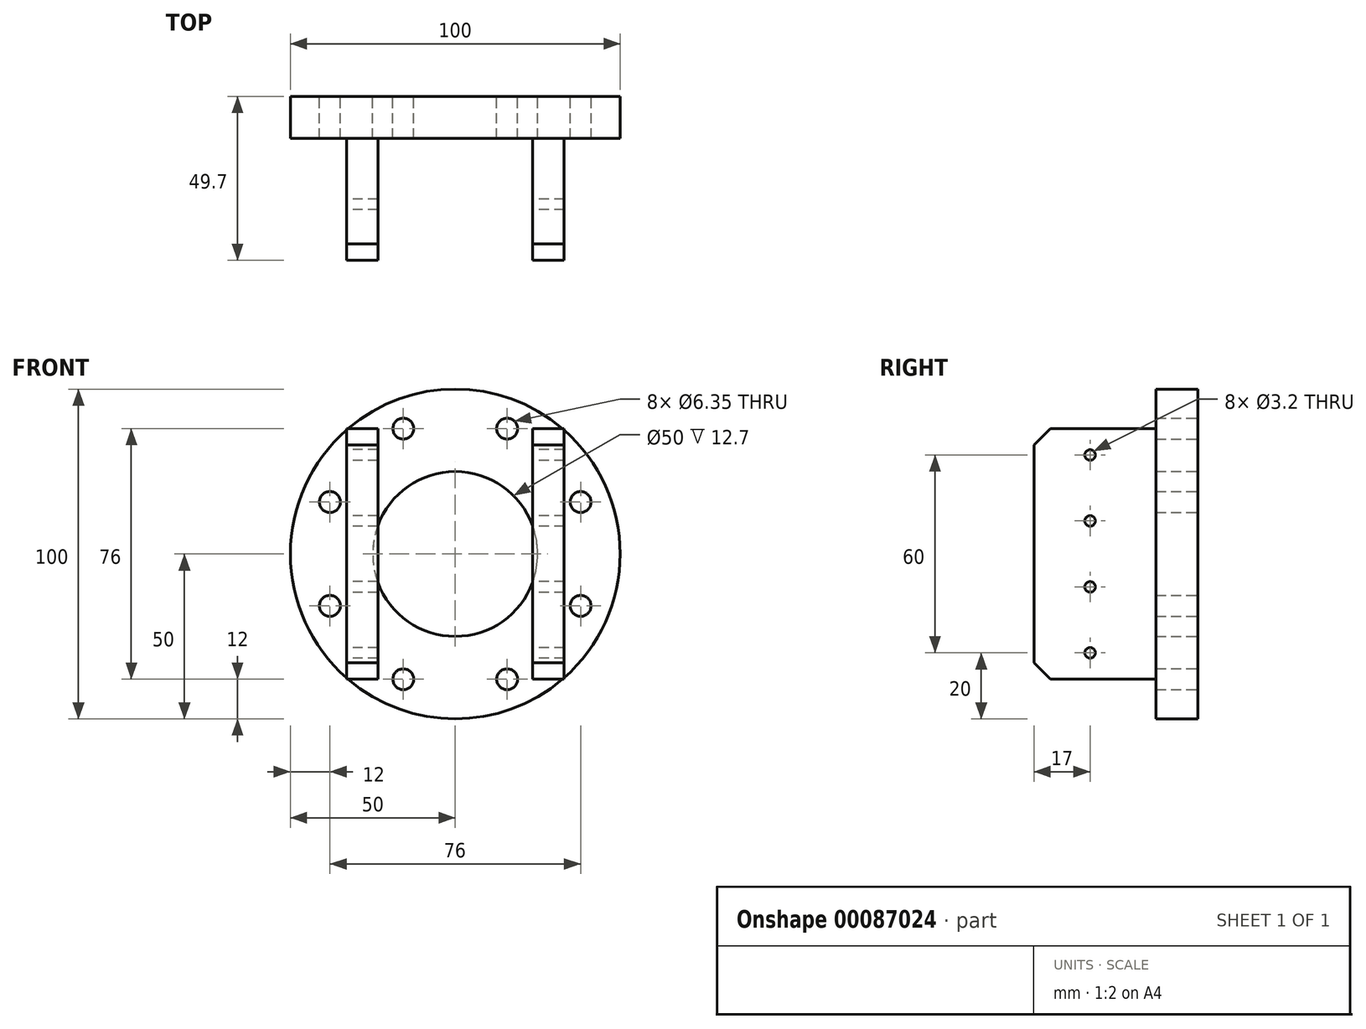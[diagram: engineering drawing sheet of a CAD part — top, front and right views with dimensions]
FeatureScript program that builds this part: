
annotation { "Feature Type Name" : "Feature", "Feature Type Description" : "" }
export const myFeature = defineFeature(function(context is Context, id is Id, definition is map)
    precondition{}
    {
        {
            var Q0;
            Q0=qCreatedBy(makeId("Front.planeOp"),FACE);
            var sketch = newSketch(context, id + "F0", { "sketchPlane" : qUnion([Q0])});
            skCircle(sketch, "E0", {"center": v(0, 0) * mm, "radius": 50 * mm});
            skCircle(sketch, "E1.cCircle", {"center": v(0, 0) * mm, "radius": 38 * mm, "construction": true});
            skLineSegment(sketch, "E1.0", {"start": v(-15.74, 38) * mm, "end": v(15.74, 38) * mm, "construction": true});
            skLineSegment(sketch, "E1.1", {"start": v(15.74, 38) * mm, "end": v(38, 15.74) * mm, "construction": true});
            skLineSegment(sketch, "E1.2", {"start": v(38, 15.74) * mm, "end": v(38, -15.74) * mm, "construction": true});
            skLineSegment(sketch, "E1.3", {"start": v(38, -15.74) * mm, "end": v(15.74, -38) * mm, "construction": true});
            skLineSegment(sketch, "E1.4", {"start": v(15.74, -38) * mm, "end": v(-15.74, -38) * mm, "construction": true});
            skLineSegment(sketch, "E1.5", {"start": v(-15.74, -38) * mm, "end": v(-38, -15.74) * mm, "construction": true});
            skLineSegment(sketch, "E1.6", {"start": v(-38, -15.74) * mm, "end": v(-38, 15.74) * mm, "construction": true});
            skLineSegment(sketch, "E1.7", {"start": v(-38, 15.74) * mm, "end": v(-15.74, 38) * mm, "construction": true});
            skPoint(sketch, "E1.0.midPoint", {"position": v(0, 38) * mm});
            skCircle(sketch, "E2", {"center": v(15.74, 38) * mm, "radius": 3.17 * mm});
            skCircle(sketch, "E3", {"center": v(38, 15.74) * mm, "radius": 3.17 * mm});
            skCircle(sketch, "E4", {"center": v(38, -15.74) * mm, "radius": 3.17 * mm});
            skCircle(sketch, "E5", {"center": v(15.74, -38) * mm, "radius": 3.17 * mm});
            skCircle(sketch, "E6", {"center": v(-15.74, -38) * mm, "radius": 3.17 * mm});
            skCircle(sketch, "E7", {"center": v(-38, -15.74) * mm, "radius": 3.17 * mm});
            skCircle(sketch, "E8", {"center": v(-38, 15.74) * mm, "radius": 3.17 * mm});
            skCircle(sketch, "E9", {"center": v(-15.74, 38) * mm, "radius": 3.17 * mm});
            skCircle(sketch, "E10", {"center": v(0, 0) * mm, "radius": 25 * mm});
            skSolve(sketch);
        }
        {
            var Q0;
            Q0 = qSketchRegion(id + "F0", true);
            extrude(context, id + "F1", {"entities" : qUnion([Q0]), "depth" : 12.7 * mm});
        }
        {
            var Q0;
            Q0=makeQuery(id+"F1.opExtrude","CAP_FACE",FACE,{"disambiguationData":[OSD([sQuery(id+"F0.wireOp",EDGE,"E0"),sQuery(id+"F0.wireOp",EDGE,"E2"),sQuery(id+"F0.wireOp",EDGE,"E3"),sQuery(id+"F0.wireOp",EDGE,"E4"),sQuery(id+"F0.wireOp",EDGE,"E5"),sQuery(id+"F0.wireOp",EDGE,"E6"),sQuery(id+"F0.wireOp",EDGE,"E7"),sQuery(id+"F0.wireOp",EDGE,"E8"),sQuery(id+"F0.wireOp",EDGE,"E9"),sQuery(id+"F0.wireOp",EDGE,"E10")])],"isStart":false});
            var sketch = newSketch(context, id + "F2", { "sketchPlane" : qUnion([Q0])});
            skLineSegment(sketch, "E11", {"start": v(0, 50) * mm, "end": v(0, -50) * mm, "construction": true});
            skLineSegment(sketch, "E12.bottom", {"start": v(-33, 38) * mm, "end": v(-23.47, 38) * mm});
            skLineSegment(sketch, "E12.top", {"start": v(-33, -38) * mm, "end": v(-23.47, -38) * mm});
            skLineSegment(sketch, "E12.left", {"start": v(-33, 38) * mm, "end": v(-33, -38) * mm});
            skLineSegment(sketch, "E12.right", {"start": v(-23.47, 38) * mm, "end": v(-23.48, -38) * mm});
            skLineSegment(sketch, "E13", {"start": v(-50, 0) * mm, "end": v(50, 0) * mm, "construction": true});
            skLineSegment(sketch, "E14.MirrorCS", {"start": v(23.48, 38) * mm, "end": v(23.48, -38) * mm});
            skLineSegment(sketch, "E15.MirrorCS", {"start": v(33, 38) * mm, "end": v(33, -38) * mm});
            skLineSegment(sketch, "E16.MirrorCS", {"start": v(33, -38) * mm, "end": v(23.47, -38) * mm});
            skLineSegment(sketch, "E17.MirrorCS", {"start": v(33, 38) * mm, "end": v(23.47, 38) * mm});
            skSolve(sketch);
        }
        {
            var Q0;
            Q0 = qSketchRegion(id + "F2", true);
            var Q1;
            Q1 = qSketchRegion(id + "F4", true);
            extrude(context, id + "F3", {"entities" : qUnion([Q0, Q1]), "operationType" : NewBodyOperationType.ADD, "depth" : 37 * mm});
        }
        {
            var Q0;
            Q0=makeQuery(id+"F3.opExtrude","SWEPT_FACE",FACE,{"disambiguationData":[OSD([sQuery(id+"F2.wireOp",EDGE,"E12.left")])]});
            var sketch = newSketch(context, id + "F4", { "sketchPlane" : qUnion([Q0])});
            skLineSegment(sketch, "E18", {"start": v(32.7, 38) * mm, "end": v(32.7, -38) * mm, "construction": true});
            skCircle(sketch, "E19", {"center": v(32.7, 30) * mm, "radius": 1.6 * mm});
            skCircle(sketch, "E20.0.1.0", {"center": v(32.7, 10) * mm, "radius": 1.6 * mm});
            skCircle(sketch, "E20.0.2.0", {"center": v(32.7, -10) * mm, "radius": 1.6 * mm});
            skCircle(sketch, "E20.0.3.0", {"center": v(32.7, -30) * mm, "radius": 1.6 * mm});
            skLineSegment(sketch, "E20.direction1", {"start": v(32.7, 30) * mm, "end": v(54.75, 30) * mm, "construction": true});
            skLineSegment(sketch, "E20.direction2", {"start": v(32.7, 30) * mm, "end": v(32.7, 10) * mm, "construction": true});
            skLineSegment(sketch, "E21", {"start": v(49.7, 0) * mm, "end": v(12.7, 0) * mm});
            skSolve(sketch);
        }
        {
            var Q0;
            Q0 = qSketchRegion(id + "F4", true);
            extrude(context, id + "F5", {"entities" : qUnion([Q0]), "operationType" : NewBodyOperationType.REMOVE, "endBound" : BoundingType.THROUGH_ALL, "oppositeDirection" : true, "depth" : 25 * mm});
        }
        {
            var Q0;
            Q0=makeQuery(id+"F3.opExtrude","CAP_EDGE",EDGE,{"disambiguationData":[OSD([sQuery(id+"F2.wireOp",EDGE,"E12.top")])],"isStart":false});
            var Q1;
            Q1=makeQuery(id+"F3.opExtrude","CAP_EDGE",EDGE,{"disambiguationData":[OSD([sQuery(id+"F2.wireOp",EDGE,"E16.MirrorCS")])],"isStart":false});
            var Q2;
            Q2=makeQuery(id+"F3.opExtrude","CAP_EDGE",EDGE,{"disambiguationData":[OSD([sQuery(id+"F2.wireOp",EDGE,"E12.bottom")])],"isStart":false});
            var Q3;
            Q3=makeQuery(id+"F3.opExtrude","CAP_EDGE",EDGE,{"disambiguationData":[OSD([sQuery(id+"F2.wireOp",EDGE,"E17.MirrorCS")])],"isStart":false});
            chamfer(context, id + "F6", {"entities" : qUnion([Q0, Q1, Q2, Q3]), "width" : 5 * mm, "tangentPropagation" : true});
        }
    });
